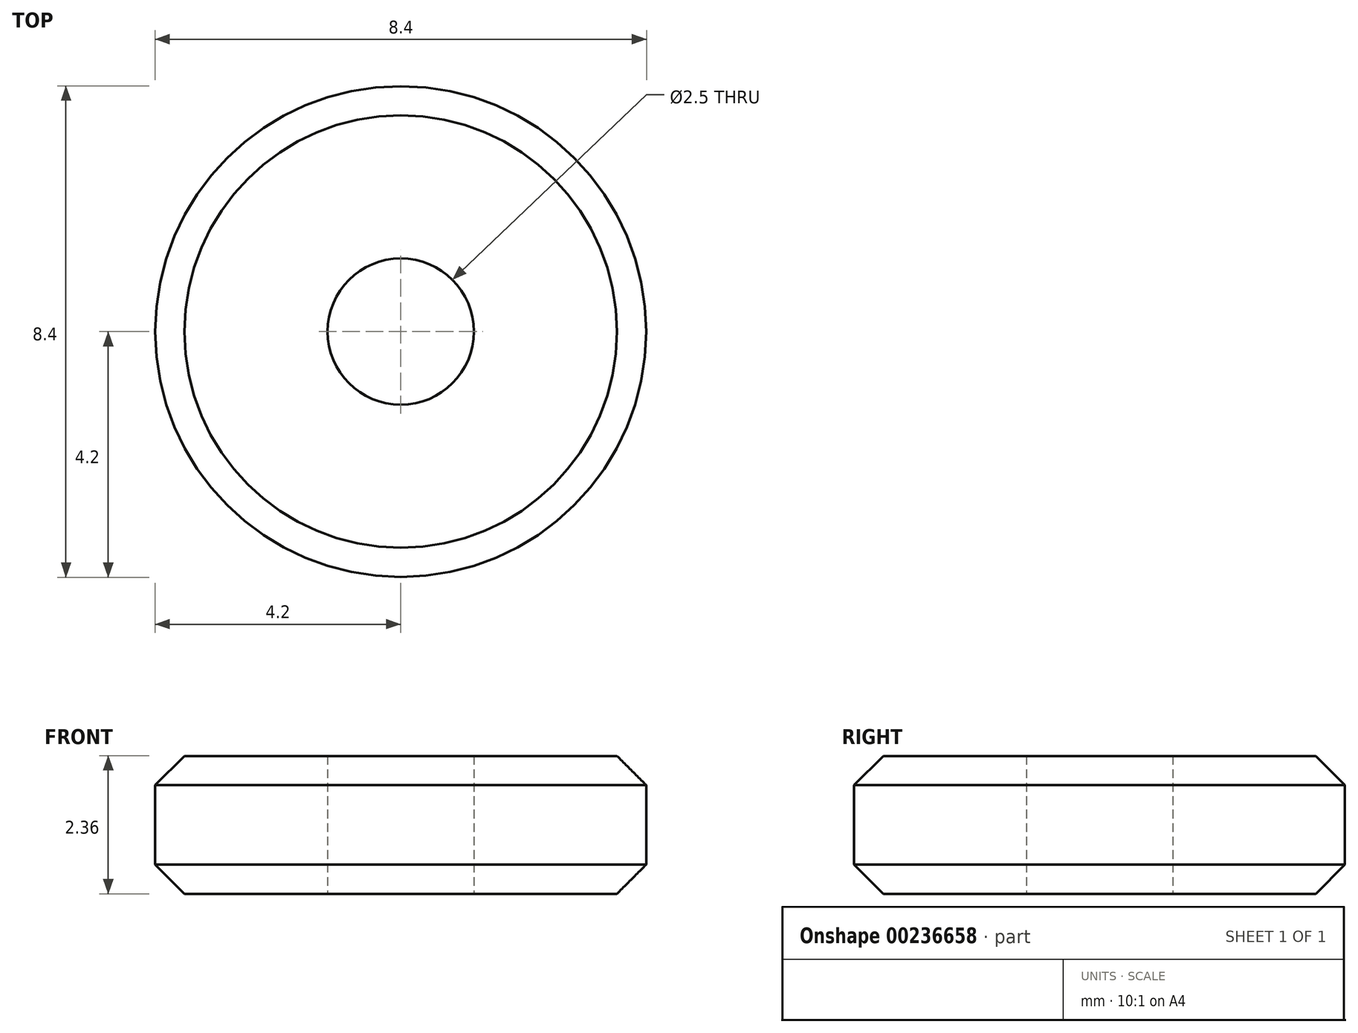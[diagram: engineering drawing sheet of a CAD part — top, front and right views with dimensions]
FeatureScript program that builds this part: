
annotation { "Feature Type Name" : "Feature", "Feature Type Description" : "" }
export const myFeature = defineFeature(function(context is Context, id is Id, definition is map)
    precondition{}
    {
        {
            assignVariable(context, id + "F0", {"name" : "scale", "anyValue" : 1 / 87});
        }
        {
            var Q0;
            Q0=qCreatedBy(makeId("Top.planeOp"),FACE);
            var sketch = newSketch(context, id + "F1", { "sketchPlane" : qUnion([Q0])});
            skCircle(sketch, "E0", {"center": v(0, 0) * mm, "radius": 4.2 * mm});
            skCircle(sketch, "E1", {"center": v(0, 0) * mm, "radius": 1.25 * mm});
            skSolve(sketch);
        }
        {
            var Q0;
            Q0=qSketchRegion(id+"F1",true);
            extrude(context, id + "F2", {"entities" : qUnion([Q0]), "depth" : 205 * getVariable(context, 'scale') * mm});
        }
        {
            var Q0;
            Q0=makeQuery(id+"F2.opExtrude","CAP_EDGE",EDGE,{"disambiguationData":[OSD([sQuery(id+"F1.wireOp",EDGE,"E0")])],"isStart":false});
            var Q1;
            Q1=makeQuery(id+"F2.opExtrude","CAP_EDGE",EDGE,{"disambiguationData":[OSD([sQuery(id+"F1.wireOp",EDGE,"E0")])],"isStart":true});
            chamfer(context, id + "F3", {"entities" : qUnion([Q0, Q1]), "width" : .5 * mm, "tangentPropagation" : true});
        }
    });
